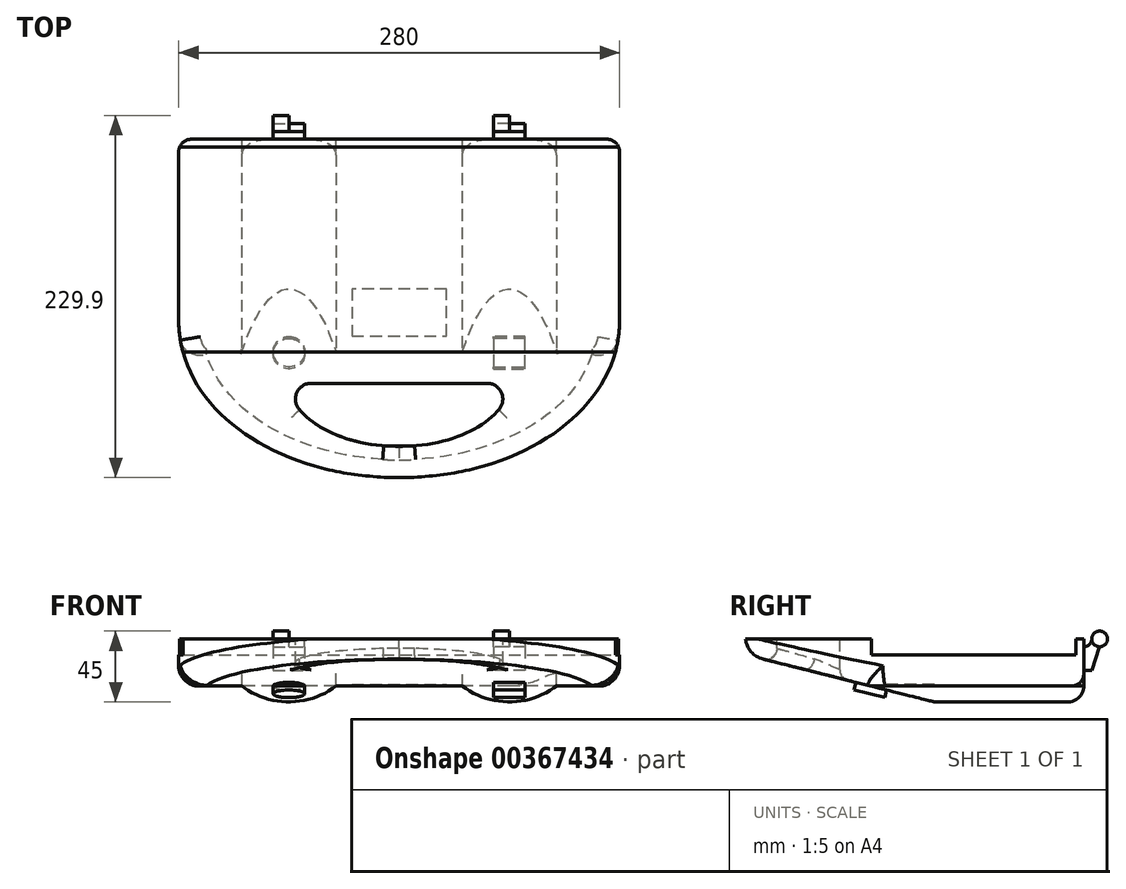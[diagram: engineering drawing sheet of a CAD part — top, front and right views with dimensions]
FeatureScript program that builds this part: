
annotation { "Feature Type Name" : "Feature", "Feature Type Description" : "" }
export const myFeature = defineFeature(function(context is Context, id is Id, definition is map)
    precondition{}
    {
        {
            var Q0;
            Q0=qCreatedBy(makeId("Front.planeOp"),FACE);
            var sketch = newSketch(context, id + "F0", { "sketchPlane" : qUnion([Q0])});
            skLineSegment(sketch, "E0", {"start": v(0, 0) * mm, "end": v(-140, 0) * mm});
            skLineSegment(sketch, "E1", {"start": v(-140, 0) * mm, "end": v(-140, -40) * mm});
            skLineSegment(sketch, "E2", {"start": v(-140, -40) * mm, "end": v(0, -40) * mm});
            skLineSegment(sketch, "E3.MirrorCS", {"start": v(140, -40) * mm, "end": v(0, -40) * mm});
            skLineSegment(sketch, "E4.MirrorCS", {"start": v(0, 0) * mm, "end": v(140, 0) * mm});
            skLineSegment(sketch, "E5.MirrorCS", {"start": v(140, 0) * mm, "end": v(140, -40) * mm});
            skSolve(sketch);
        }
        {
            var Q0;
            Q0=makeQuery(id+"F0.imprint","IMPRINT",FACE,{"disambiguationData":[TD([[makeQuery(id+"F0.imprint","IMPRINT",EDGE,{"derivedFrom":sQuery(id+"F0.wireOp",EDGE,"E0")}),1.0]])]});
            extrude(context, id + "F1", {"entities" : qUnion([Q0]), "endBound" : BoundingType.SYMMETRIC, "depth" : 240 * mm});
        }
        {
            var Q0;
            Q0=makeQuery(id+"F1.opExtrude","SWEPT_FACE",FACE,{"disambiguationData":[OSD([sQuery(id+"F0.wireOp",EDGE,"E5.MirrorCS")])]});
            var sketch = newSketch(context, id + "F2", { "sketchPlane" : qUnion([Q0])});
            skLineSegment(sketch, "E6", {"start": v(-120, 0) * mm, "end": v(-120, -10) * mm});
            skLineSegment(sketch, "E7", {"start": v(-120, -10) * mm, "end": v(-40, -30) * mm});
            skLineSegment(sketch, "E8", {"start": v(-40, -30) * mm, "end": v(0, -40) * mm});
            skLineSegment(sketch, "E9", {"start": v(0, -40) * mm, "end": v(0, -60.45) * mm});
            skLineSegment(sketch, "E10", {"start": v(0, -60.45) * mm, "end": v(-153.05, -60.45) * mm});
            skLineSegment(sketch, "E11", {"start": v(-153.05, -60.45) * mm, "end": v(-153.05, 0) * mm});
            skLineSegment(sketch, "E12", {"start": v(-153.05, 0) * mm, "end": v(-120, 0) * mm});
            skSolve(sketch);
        }
        {
            var Q0;
            Q0=makeQuery(id+"F1.opExtrude","SWEPT_FACE",FACE,{"disambiguationData":[OSD([sQuery(id+"F0.wireOp",EDGE,"E0"),sQuery(id+"F0.wireOp",EDGE,"E4.MirrorCS")])]});
            var sketch = newSketch(context, id + "F3", { "sketchPlane" : qUnion([Q0])});
            skFitSpline(sketch, "E13", {"points": [v(0, -120) * mm, v(-140, -20) * mm], "startDerivative": vector(-228.5, 0) * mm, "endDerivative": vector(0, 173.14) * mm});
            skFitSpline(sketch, "E14.MirrorCS", {"points": [v(0, -120) * mm, v(140, -20) * mm], "startDerivative": vector(228.5, 0) * mm, "endDerivative": vector(0, 173.14) * mm});
            skLineSegment(sketch, "E15", {"start": v(-140, -20) * mm, "end": v(-187.85, -20) * mm});
            skLineSegment(sketch, "E16", {"start": v(-187.85, -20) * mm, "end": v(-187.85, -152.6) * mm});
            skLineSegment(sketch, "E17", {"start": v(-187.85, -152.6) * mm, "end": v(0, -152.6) * mm});
            skLineSegment(sketch, "E18.MirrorCS", {"start": v(187.85, -152.6) * mm, "end": v(0, -152.6) * mm});
            skLineSegment(sketch, "E19.MirrorCS", {"start": v(140, -20) * mm, "end": v(187.85, -20) * mm});
            skLineSegment(sketch, "E20.MirrorCS", {"start": v(187.85, -20) * mm, "end": v(187.85, -152.6) * mm});
            skSolve(sketch);
        }
        {
            var Q0;
            Q0=makeQuery(id+"F1.opExtrude","CAP_FACE",FACE,{"disambiguationData":[OSD([sQuery(id+"F0.wireOp",EDGE,"E0"),sQuery(id+"F0.wireOp",EDGE,"E1"),sQuery(id+"F0.wireOp",EDGE,"E2"),sQuery(id+"F0.wireOp",EDGE,"E3.MirrorCS"),sQuery(id+"F0.wireOp",EDGE,"E4.MirrorCS"),sQuery(id+"F0.wireOp",EDGE,"E5.MirrorCS")])],"isStart":false});
            var sketch = newSketch(context, id + "F4", { "sketchPlane" : qUnion([Q0])});
            skLineSegment(sketch, "E21", {"start": v(-140, -30) * mm, "end": v(-100, -30) * mm});
            skArc(sketch, "E22", {"start": v(-100, -30) * mm, "mid": v(-70, -40) * mm, "end": v(-40, -30) * mm});
            skLineSegment(sketch, "E23", {"start": v(-140, -30) * mm, "end": v(-177.9, -30) * mm});
            skLineSegment(sketch, "E24", {"start": v(-177.9, -30) * mm, "end": v(-177.9, -89.34) * mm});
            skLineSegment(sketch, "E25", {"start": v(-177.9, -89.34) * mm, "end": v(0, -89.34) * mm});
            skPoint(sketch, "E26.endSnap0", {"position": v(0, -40) * mm});
            skLineSegment(sketch, "E27", {"start": v(0, -30) * mm, "end": v(-40, -30) * mm});
            skLineSegment(sketch, "E28.MirrorCS", {"start": v(140, -30) * mm, "end": v(100, -30) * mm});
            skArc(sketch, "E29.MirrorCS", {"start": v(100, -30) * mm, "mid": v(70, -40) * mm, "end": v(40, -30) * mm});
            skLineSegment(sketch, "E30.MirrorCS", {"start": v(140, -30) * mm, "end": v(177.9, -30) * mm});
            skLineSegment(sketch, "E31.MirrorCS", {"start": v(177.9, -30) * mm, "end": v(177.9, -89.34) * mm});
            skLineSegment(sketch, "E32.MirrorCS", {"start": v(177.9, -89.34) * mm, "end": v(0, -89.34) * mm});
            skLineSegment(sketch, "E33.MirrorCS", {"start": v(0, -30) * mm, "end": v(40, -30) * mm});
            skSolve(sketch);
        }
        {
            var Q0;
            {var subQ4=sQuery(id+"F3.wireOp",EDGE,"E13");Q0=makeQuery(id+"F3.imprint","IMPRINT",FACE,{"disambiguationData":[TD([[makeQuery(id+"F3.imprint","IMPRINT",EDGE,{"derivedFrom":subQ4}),-1.0]])]});}
            var sketch = newSketch(context, id + "F5", { "sketchPlane" : qUnion([Q0])});
            skFitSpline(sketch, "E34", {"points": [v(0, -100) * mm, v(-70, -60) * mm], "startDerivative": vector(-116.82, -1.18) * mm, "endDerivative": vector(-0.75, 63.41) * mm});
            skLineSegment(sketch, "E35", {"start": v(-55.84, -60) * mm, "end": v(0, -60) * mm});
            skLineSegment(sketch, "E36.MirrorCS", {"start": v(55.84, -60) * mm, "end": v(0, -60) * mm});
            skFitSpline(sketch, "E37.MirrorCS", {"points": [v(0, -100) * mm, v(70, -60) * mm], "startDerivative": vector(116.82, -1.18) * mm, "endDerivative": vector(0.75, 63.41) * mm});
            skArc(sketch, "E38.filletArc", {"start": v(-55.84, -60) * mm, "mid": v(-64.84, -65.66) * mm, "end": v(-63.66, -76.23) * mm});
            skArc(sketch, "E39.filletArc", {"start": v(63.66, -76.23) * mm, "mid": v(64.84, -65.66) * mm, "end": v(55.84, -60) * mm});
            skSolve(sketch);
        }
        {
            var Q0;
            Q0 = qSketchRegion(id + "F3", true);
            extrude(context, id + "F6", {"entities" : qUnion([Q0]), "operationType" : NewBodyOperationType.REMOVE, "oppositeDirection" : true, "depth" : 100 * mm});
        }
        {
            var Q0;
            Q0 = qSketchRegion(id + "F4", true);
            extrude(context, id + "F7", {"entities" : qUnion([Q0]), "operationType" : NewBodyOperationType.REMOVE, "oppositeDirection" : true, "depth" : 400 * mm});
        }
        {
            var Q0;
            Q0 = qSketchRegion(id + "F2", true);
            extrude(context, id + "F8", {"entities" : qUnion([Q0]), "operationType" : NewBodyOperationType.REMOVE, "oppositeDirection" : true, "depth" : 300 * mm});
        }
        {
            var Q0;
            Q0 = qSketchRegion(id + "F5", true);
            extrude(context, id + "F9", {"entities" : qUnion([Q0]), "operationType" : NewBodyOperationType.REMOVE, "oppositeDirection" : true, "depth" : 25 * mm});
        }
        {
            var Q0;
            Q0=makeQuery(id+"F1.opExtrude","SWEPT_FACE",FACE,{"disambiguationData":[OSD([sQuery(id+"F0.wireOp",EDGE,"E5.MirrorCS")])]});
            var sketch = newSketch(context, id + "F10", { "sketchPlane" : qUnion([Q0])});
            skLineSegment(sketch, "E40", {"start": v(-40, 0) * mm, "end": v(-40, -10) * mm});
            skLineSegment(sketch, "E41", {"start": v(-40, -10) * mm, "end": v(90, -10) * mm});
            skLineSegment(sketch, "E42", {"start": v(90, -10) * mm, "end": v(90, 19.27) * mm});
            skLineSegment(sketch, "E43", {"start": v(90, 19.27) * mm, "end": v(-40, 19.27) * mm});
            skLineSegment(sketch, "E44", {"start": v(-40, 19.27) * mm, "end": v(-40, 0) * mm});
            skSolve(sketch);
        }
        {
            var Q0;
            Q0 = qSketchRegion(id + "F10", true);
            extrude(context, id + "F11", {"entities" : qUnion([Q0]), "operationType" : NewBodyOperationType.REMOVE, "oppositeDirection" : true, "depth" : 300 * mm});
        }
        {
            var Q0;
            Q0=makeQuery(id+"F1.opExtrude","SWEPT_FACE",FACE,{"disambiguationData":[OSD([sQuery(id+"F0.wireOp",EDGE,"E5.MirrorCS")])]});
            var sketch = newSketch(context, id + "F12", { "sketchPlane" : qUnion([Q0])});
            skLineSegment(sketch, "E45", {"start": v(95, 0) * mm, "end": v(95, -52.5) * mm});
            skLineSegment(sketch, "E46", {"start": v(95, -52.5) * mm, "end": v(129.76, -52.5) * mm});
            skLineSegment(sketch, "E47", {"start": v(129.76, -52.5) * mm, "end": v(129.76, 18.92) * mm});
            skLineSegment(sketch, "E48", {"start": v(129.76, 18.92) * mm, "end": v(95, 18.92) * mm});
            skLineSegment(sketch, "E49", {"start": v(95, 18.92) * mm, "end": v(95, 0) * mm});
            skSolve(sketch);
        }
        {
            var Q0;
            Q0 = qSketchRegion(id + "F12", true);
            extrude(context, id + "F13", {"entities" : qUnion([Q0]), "operationType" : NewBodyOperationType.REMOVE, "oppositeDirection" : true, "depth" : 300 * mm});
        }
        {
            var Q0;
            Q0=makeQuery(id+"F13.boolean.opBoolean","COPY",FACE,{"derivedFrom":makeQuery(id+"F13.opExtrude","SWEPT_FACE",FACE,{"disambiguationData":[OSD([sQuery(id+"F12.wireOp",EDGE,"E45"),sQuery(id+"F12.wireOp",EDGE,"E49")])]})});
            var sketch = newSketch(context, id + "F14", { "sketchPlane" : qUnion([Q0])});
            skLineSegment(sketch, "E50", {"start": v(-70, -40) * mm, "end": v(-70, 0) * mm});
            skLineSegment(sketch, "E51", {"start": v(-70, -20) * mm, "end": v(-140, -20) * mm});
            skLineSegment(sketch, "E52", {"start": v(70, -40) * mm, "end": v(70, 0) * mm});
            skLineSegment(sketch, "E53", {"start": v(70, -20) * mm, "end": v(140, -20) * mm});
            skSolve(sketch);
        }
        {
            var Q0;
            Q0=sQuery(id+"F14.wireOp",EDGE,"E51");
            var Q1;
            Q1=sQuery(id+"F14.wireOp",VERTEX,"E51.start");
            cPlane(context, id + "F15", {"entities" : qUnion([Q0, Q1]), "cplaneType" : CPlaneType.LINE_POINT, "offset" : 25 * mm, "width" : 150 * mm, "height" : 150 * mm});
        }
        {
            var Q0;
            Q0=qCreatedBy(id+"F15.planeOp",FACE);
            var sketch = newSketch(context, id + "F16", { "sketchPlane" : qUnion([Q0])});
            skLineSegment(sketch, "E54", {"start": v(95, -5) * mm, "end": v(95, -20) * mm});
            skLineSegment(sketch, "E55", {"start": v(95, -20) * mm, "end": v(100, -20) * mm});
            skLineSegment(sketch, "E56", {"start": v(95, -5) * mm, "end": v(95, -5) * mm});
            skLineSegment(sketch, "E57", {"start": v(95, -20) * mm, "end": v(0, -20) * mm});
            skLineSegment(sketch, "E58", {"start": v(0, -20) * mm, "end": v(0, 0) * mm});
            skLineSegment(sketch, "E59", {"start": v(105, -5) * mm, "end": v(100, -20) * mm});
            skLineSegment(sketch, "E60", {"start": v(105, -5) * mm, "end": v(105, 0) * mm});
            skCircle(sketch, "E61", {"center": v(105, 0) * mm, "radius": 5 * mm});
            skLineSegment(sketch, "E62", {"start": v(100, 0) * mm, "end": v(100, 0) * mm});
            skPoint(sketch, "E63.newPointA", {"position": v(100, -5) * mm});
            skPoint(sketch, "E63.newPointB", {"position": v(105, -5) * mm});
            skArc(sketch, "E63.filletArc", {"start": v(95, -5) * mm, "mid": v(98.54, -3.54) * mm, "end": v(100, 0) * mm});
            skSolve(sketch);
        }
        {
            var Q0;
            Q0=sQuery(id+"F14.wireOp",EDGE,"E53");
            var Q1;
            Q1=sQuery(id+"F14.wireOp",VERTEX,"E53.start");
            cPlane(context, id + "F17", {"entities" : qUnion([Q0, Q1]), "cplaneType" : CPlaneType.LINE_POINT, "offset" : 25 * mm, "width" : 150 * mm, "height" : 150 * mm});
        }
        {
            var Q0;
            Q0=qCreatedBy(id+"F17.planeOp",FACE);
            var sketch = newSketch(context, id + "F18", { "sketchPlane" : qUnion([Q0])});
            skLineSegment(sketch, "E64", {"start": v(-95, -5) * mm, "end": v(-95, -20) * mm});
            skLineSegment(sketch, "E65", {"start": v(-95, -20) * mm, "end": v(-100, -20) * mm});
            skLineSegment(sketch, "E66", {"start": v(-100, -20) * mm, "end": v(-105, -5) * mm});
            skLineSegment(sketch, "E67", {"start": v(-95, -5) * mm, "end": v(-95, -5) * mm});
            skPoint(sketch, "E68.newPointA", {"position": v(-100, -5) * mm});
            skPoint(sketch, "E68.newPointB", {"position": v(-105, -5) * mm});
            skLineSegment(sketch, "E69", {"start": v(-95, -20) * mm, "end": v(0, -20) * mm});
            skLineSegment(sketch, "E70", {"start": v(0, -20) * mm, "end": v(0, 0) * mm});
            skLineSegment(sketch, "E71", {"start": v(-105, -5) * mm, "end": v(-105, 0) * mm});
            skCircle(sketch, "E72", {"center": v(-105, 0) * mm, "radius": 5 * mm});
            skLineSegment(sketch, "E73", {"start": v(-100, 0) * mm, "end": v(-100, 0) * mm});
            skArc(sketch, "E74.filletArc", {"start": v(-100, 0) * mm, "mid": v(-98.54, -3.54) * mm, "end": v(-95, -5) * mm});
            skSolve(sketch);
        }
        {
            var Q0;
            Q0=makeQuery(id+"F8.boolean.opBoolean","COPY",FACE,{"derivedFrom":makeQuery(id+"F8.opExtrude","SWEPT_FACE",FACE,{"disambiguationData":[OSD([sQuery(id+"F2.wireOp",EDGE,"E7"),sQuery(id+"F2.wireOp",EDGE,"E8")])]})});
            var sketch = newSketch(context, id + "F19", { "sketchPlane" : qUnion([Q0])});
            skLineSegment(sketch, "E75", {"start": v(-70, -9.7) * mm, "end": v(-70, 31.53) * mm});
            skCircle(sketch, "E76", {"center": v(-70, 31.53) * mm, "radius": 10 * mm});
            skLineSegment(sketch, "E77", {"start": v(70, -9.7) * mm, "end": v(70, 31.53) * mm});
            skLineSegment(sketch, "E78", {"start": v(70, 31.53) * mm, "end": v(70, 21.53) * mm});
            skLineSegment(sketch, "E79", {"start": v(70, 21.53) * mm, "end": v(60, 21.53) * mm});
            skLineSegment(sketch, "E80", {"start": v(60, 21.53) * mm, "end": v(60, 41.53) * mm});
            skLineSegment(sketch, "E81", {"start": v(60, 41.53) * mm, "end": v(80, 41.53) * mm});
            skLineSegment(sketch, "E82", {"start": v(80, 41.53) * mm, "end": v(80, 21.53) * mm});
            skLineSegment(sketch, "E83", {"start": v(80, 21.53) * mm, "end": v(60, 21.53) * mm});
            skLineSegment(sketch, "E84", {"start": v(-40, 31.53) * mm, "end": v(-40, 52.15) * mm});
            skLineSegment(sketch, "E85", {"start": v(-40, 52.15) * mm, "end": v(40, 52.15) * mm});
            skLineSegment(sketch, "E86", {"start": v(40, 52.15) * mm, "end": v(40, 31.53) * mm});
            skLineSegment(sketch, "E87", {"start": v(40, 31.53) * mm, "end": v(-40, 31.53) * mm});
            skSolve(sketch);
        }
        {
            var Q0;
            {var subQ3=sQuery(id+"F19.wireOp",EDGE,"E80");Q0=makeQuery(id+"F19.imprint","IMPRINT",FACE,{"disambiguationData":[TD([[makeQuery(id+"F19.imprint","IMPRINT",EDGE,{"derivedFrom":subQ3}),-1.0]])]});}
            var Q1;
            Q1=makeQuery(id+"F19.imprint","IMPRINT",FACE,{"disambiguationData":[TD([[makeQuery(id+"F19.imprint","IMPRINT",EDGE,{"derivedFrom":sQuery(id+"F19.wireOp",EDGE,"E76")}),1.0]])]});
            extrude(context, id + "F20", {"entities" : qUnion([Q0, Q1]), "operationType" : NewBodyOperationType.ADD, "depth" : 5 * mm});
        }
        {
            var Q0;
            Q0=makeQuery(id+"F8.boolean.opBoolean","INTERSECT",EDGE,{"derivedFrom":[makeQuery(id+"F6.boolean.opBoolean","COPY",FACE,{"derivedFrom":makeQuery(id+"F6.opExtrude","SWEPT_FACE",FACE,{"disambiguationData":[OSD([sQuery(id+"F3.wireOp",EDGE,"E14.MirrorCS")])]})}),makeQuery(id+"F8.opExtrude","SWEPT_FACE",FACE,{"disambiguationData":[OSD([sQuery(id+"F2.wireOp",EDGE,"E7"),sQuery(id+"F2.wireOp",EDGE,"E8")])]})]});
            fillet(context, id + "F21", {"entities" : qUnion([Q0]), "radius" : 15 * mm, "tangentPropagation" : true, "allowEdgeOverflow" : false});
        }
        {
            var Q0;
            Q0=makeQuery(id+"F7.boolean.opBoolean","INTERSECT",EDGE,{"derivedFrom":[makeQuery(id+"F1.opExtrude","SWEPT_FACE",FACE,{"disambiguationData":[OSD([sQuery(id+"F0.wireOp",EDGE,"E5.MirrorCS")])]}),makeQuery(id+"F7.opExtrude","SWEPT_FACE",FACE,{"disambiguationData":[OSD([sQuery(id+"F4.wireOp",EDGE,"E28.MirrorCS"),sQuery(id+"F4.wireOp",EDGE,"E30.MirrorCS")])]})]});
            fillet(context, id + "F22", {"entities" : qUnion([Q0]), "radius" : 13 * mm, "tangentPropagation" : true, "allowEdgeOverflow" : false});
        }
        {
            var Q0;
            Q0=makeQuery(id+"F7.boolean.opBoolean","INTERSECT",EDGE,{"derivedFrom":[makeQuery(id+"F1.opExtrude","SWEPT_FACE",FACE,{"disambiguationData":[OSD([sQuery(id+"F0.wireOp",EDGE,"E1")])]}),makeQuery(id+"F7.opExtrude","SWEPT_FACE",FACE,{"disambiguationData":[OSD([sQuery(id+"F4.wireOp",EDGE,"E21"),sQuery(id+"F4.wireOp",EDGE,"E23")])]})]});
            fillet(context, id + "F23", {"entities" : qUnion([Q0]), "radius" : 13 * mm, "tangentPropagation" : true, "allowEdgeOverflow" : false});
        }
        {
            var Q0;
            Q0=makeQuery(id+"F9.boolean.opBoolean","INTERSECT",EDGE,{"derivedFrom":[makeQuery(id+"F8.boolean.opBoolean","COPY",FACE,{"derivedFrom":makeQuery(id+"F8.opExtrude","SWEPT_FACE",FACE,{"disambiguationData":[OSD([sQuery(id+"F2.wireOp",EDGE,"E7"),sQuery(id+"F2.wireOp",EDGE,"E8")])]})}),makeQuery(id+"F9.opExtrude","SWEPT_FACE",FACE,{"disambiguationData":[OSD([sQuery(id+"F5.wireOp",EDGE,"E34")])]})]});
            fillet(context, id + "F24", {"entities" : qUnion([Q0]), "radius" : 7 * mm, "tangentPropagation" : true, "allowEdgeOverflow" : false});
        }
        {
            var Q0;
            Q0=makeQuery(id+"F13.boolean.opBoolean","INTERSECT",EDGE,{"derivedFrom":[makeQuery(id+"F7.boolean.opBoolean","COPY",FACE,{"derivedFrom":makeQuery(id+"F7.opExtrude","SWEPT_FACE",FACE,{"disambiguationData":[OSD([sQuery(id+"F4.wireOp",EDGE,"E22")])]})}),makeQuery(id+"F13.opExtrude","SWEPT_FACE",FACE,{"disambiguationData":[OSD([sQuery(id+"F12.wireOp",EDGE,"E45"),sQuery(id+"F12.wireOp",EDGE,"E49")])]})]});
            fillet(context, id + "F25", {"entities" : qUnion([Q0]), "radius" : 10 * mm, "tangentPropagation" : true, "allowEdgeOverflow" : false});
        }
        {
            var Q0;
            Q0=makeQuery(id+"F13.boolean.opBoolean","INTERSECT",EDGE,{"derivedFrom":[makeQuery(id+"F7.boolean.opBoolean","COPY",FACE,{"derivedFrom":makeQuery(id+"F7.opExtrude","SWEPT_FACE",FACE,{"disambiguationData":[OSD([sQuery(id+"F4.wireOp",EDGE,"E29.MirrorCS")])]})}),makeQuery(id+"F13.opExtrude","SWEPT_FACE",FACE,{"disambiguationData":[OSD([sQuery(id+"F12.wireOp",EDGE,"E45"),sQuery(id+"F12.wireOp",EDGE,"E49")])]})]});
            fillet(context, id + "F26", {"entities" : qUnion([Q0]), "radius" : 10 * mm, "tangentPropagation" : true, "allowEdgeOverflow" : false});
        }
        {
            var Q0;
            Q0=makeQuery(id+"F13.boolean.opBoolean","INTERSECT",EDGE,{"derivedFrom":[makeQuery(id+"F7.boolean.opBoolean","COPY",FACE,{"derivedFrom":makeQuery(id+"F7.opExtrude","SWEPT_FACE",FACE,{"disambiguationData":[OSD([sQuery(id+"F4.wireOp",EDGE,"E27"),sQuery(id+"F4.wireOp",EDGE,"E33.MirrorCS")])]})}),makeQuery(id+"F13.opExtrude","SWEPT_FACE",FACE,{"disambiguationData":[OSD([sQuery(id+"F12.wireOp",EDGE,"E45"),sQuery(id+"F12.wireOp",EDGE,"E49")])]})]});
            fillet(context, id + "F27", {"entities" : qUnion([Q0]), "radius" : 8 * mm, "tangentPropagation" : true, "allowEdgeOverflow" : false});
        }
        {
            var Q0;
            Q0=makeQuery(id+"F7.boolean.opBoolean","COPY",FACE,{"derivedFrom":makeQuery(id+"F7.opExtrude","SWEPT_FACE",FACE,{"disambiguationData":[OSD([sQuery(id+"F4.wireOp",EDGE,"E27"),sQuery(id+"F4.wireOp",EDGE,"E33.MirrorCS")])]})});
            var sketch = newSketch(context, id + "F28", { "sketchPlane" : qUnion([Q0])});
            skLineSegment(sketch, "E88", {"start": v(0, 40) * mm, "end": v(0, 30) * mm});
            skLineSegment(sketch, "E89", {"start": v(0, 30) * mm, "end": v(30, 30) * mm});
            skLineSegment(sketch, "E90", {"start": v(30, 30) * mm, "end": v(30, 0) * mm});
            skLineSegment(sketch, "E91", {"start": v(30, 0) * mm, "end": v(-30, 0) * mm});
            skLineSegment(sketch, "E92", {"start": v(-30, 0) * mm, "end": v(-30, 30) * mm});
            skLineSegment(sketch, "E93", {"start": v(-30, 30) * mm, "end": v(0, 30) * mm});
            skSolve(sketch);
        }
        {
            var Q0;
            Q0=makeQuery(id+"F28.imprint","IMPRINT",FACE,{"disambiguationData":[TD([[makeQuery(id+"F28.imprint","IMPRINT",EDGE,{"derivedFrom":sQuery(id+"F28.wireOp",EDGE,"E89")}),-1.0]])]});
            extrude(context, id + "F29", {"entities" : qUnion([Q0]), "operationType" : NewBodyOperationType.REMOVE, "oppositeDirection" : true, "depth" : 1 * mm});
        }
        {
            var Q0;
            Q0=makeQuery(id+"F18.imprint","IMPRINT",FACE,{"disambiguationData":[TD([[makeQuery(id+"F18.imprint","IMPRINT",EDGE,{"derivedFrom":sQuery(id+"F18.wireOp",EDGE,"E64")}),-1.0]])]});
            extrude(context, id + "F30", {"entities" : qUnion([Q0]), "operationType" : NewBodyOperationType.ADD, "endBound" : BoundingType.SYMMETRIC, "depth" : 20 * mm});
        }
        {
            var Q0;
            {var subQ0=sQuery(id+"F18.wireOp",EDGE,"E72");var subQ1=makeQuery(id+"F18.imprint","INTERSECT",VERTEX,{"derivedFrom":[sQuery(id+"F18.wireOp",EDGE,"E66"),subQ0]});Q0=makeQuery(id+"F18.imprint","IMPRINT",FACE,{"disambiguationData":[TD([[makeQuery(id+"F18.imprint","IMPRINT",EDGE,{"disambiguationData":[TD([[subQ1,1.0]])],"derivedFrom":subQ0}),1.0]])]});}
            extrude(context, id + "F31", {"entities" : qUnion([Q0]), "operationType" : NewBodyOperationType.ADD, "depth" : 10 * mm});
        }
        {
            var Q0;
            Q0=makeQuery(id+"F16.imprint","IMPRINT",FACE,{"disambiguationData":[TD([[makeQuery(id+"F16.imprint","IMPRINT",EDGE,{"derivedFrom":sQuery(id+"F16.wireOp",EDGE,"E54")}),1.0]])]});
            extrude(context, id + "F32", {"entities" : qUnion([Q0]), "operationType" : NewBodyOperationType.ADD, "endBound" : BoundingType.SYMMETRIC, "depth" : 20 * mm});
        }
        {
            var Q0;
            {var subQ0=sQuery(id+"F16.wireOp",EDGE,"E61");var subQ1=makeQuery(id+"F16.imprint","INTERSECT",VERTEX,{"derivedFrom":[sQuery(id+"F16.wireOp",EDGE,"E59"),subQ0]});Q0=makeQuery(id+"F16.imprint","IMPRINT",FACE,{"disambiguationData":[TD([[makeQuery(id+"F16.imprint","IMPRINT",EDGE,{"disambiguationData":[TD([[subQ1,1.0]])],"derivedFrom":subQ0}),1.0]])]});}
            extrude(context, id + "F33", {"entities" : qUnion([Q0]), "operationType" : NewBodyOperationType.ADD, "oppositeDirection" : true, "depth" : 10 * mm});
        }
    });
